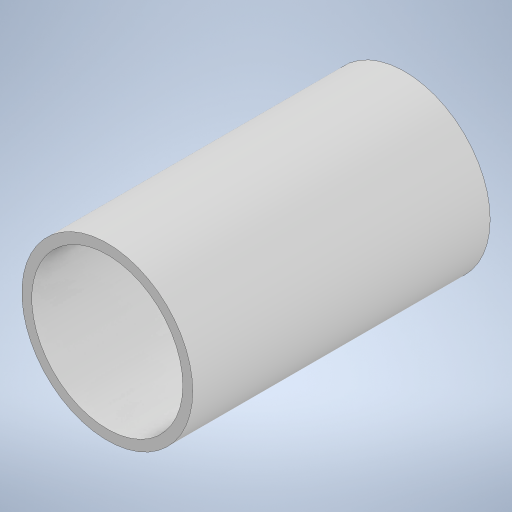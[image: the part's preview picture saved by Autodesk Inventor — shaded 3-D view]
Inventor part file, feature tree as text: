
AUTODESK INVENTOR PART (.ipt)
format: ipt  version: 2023 (Build 270158030, 158C)  size: 204,800 bytes
history: native  units: in
note: dims shown in document units (in); Inventor stores cm internally (conversion verified against a paired STEP export)
features: extrude x1, sketch x1
ambient origin geometry x8: Origin, YZ Plane, XZ Plane, XY Plane, X Axis, Y Axis, Z Axis, Center Point
bodies: Solid1 (feature_tree)
feature tree (2):
  extrude  "Extrusion1"  Depth=5.9055in
  sketch  "Sketch1"  dims[d0=3.0in d1=0.1969in d2=5.9055in d3=0.0in]
